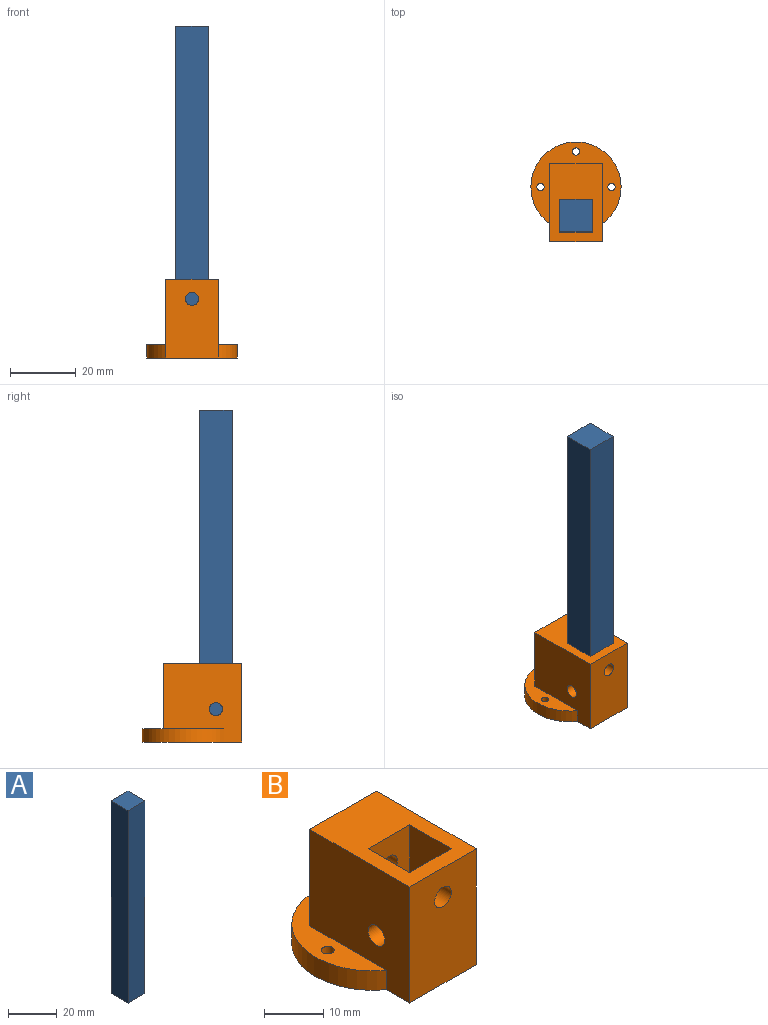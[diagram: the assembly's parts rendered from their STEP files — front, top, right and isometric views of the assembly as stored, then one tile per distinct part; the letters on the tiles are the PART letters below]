
ASSEMBLY  parts=2 mates=1
PART A: 6 faces, bbox 9.9x9.9x97.1 mm
  f0: plane 97.1x9.9mm, normal (1,0,0), area 961.3mm2, adj f1,f3,f4,f5
  f1: plane 97.1x9.9mm, normal (0,1,0), area 961.3mm2, adj f0,f2,f4,f5
  f2: plane 97.1x9.9mm, normal (-1,0,0), area 961.3mm2, adj f1,f3,f4,f5
  f3: plane 97.1x9.9mm, normal (0,-1,0), area 961.3mm2, adj f0,f2,f4,f5
  f4: plane 9.9x9.9mm, normal (0,0,1), area 98mm2, adj f0,f1,f2,f3
  f5: plane 9.9x9.9mm, normal (0,0,-1), area 98mm2, adj f0,f1,f2,f3
PART B: 25 faces, bbox 27.5x30.5x24 mm
  f0: cylinder r=1.11mm len=2.3mm, axis (0,0,-1), area 16mm2, adj f8,f24
  f1: plane 27.47x24.94mm, normal (0,0,1), area 261.6mm2, adj f3,f5,f6,f7,f10,f11,f22
  f2: plane 9.9x9.9mm, normal (0,0,1), area 85.4mm2, adj f13,f14,f15,f16,f23
  f3: cylinder r=13.74mm len=27.47mm, axis (0,0,-1), area 277.4mm2, adj f1,f8,f10,f11
  f4: cylinder r=5mm len=10mm, axis (0,0,-1), area 15.7mm2, adj f8,f9
  f5: cylinder r=1.11mm len=4mm, axis (0,0,-1), area 27.9mm2, adj f1,f8
  f6: cylinder r=1.11mm len=4mm, axis (0,0,-1), area 27.9mm2, adj f1,f8
  f7: cylinder r=1.11mm len=4mm, axis (0,0,-1), area 27.9mm2, adj f1,f8
  f8: plane 30.47x27.47mm, normal (0,0,-1), area 559.2mm2, adj f0,f3,f4,f5,f6,f7,f10,f11
  f9: plane 10x10mm, normal (0,0,-1), area 78.5mm2, adj f4
  f10: plane 24x23.9mm, normal (1,0,0), area 487.6mm2, adj f1,f3,f8,f12,f17,f19,f22
  f11: plane 24x23.9mm, normal (-1,0,0), area 487.6mm2, adj f1,f3,f8,f12,f17,f18,f22
  f12: plane 24x15.9mm, normal (0,-1,0), area 369mm2, adj f8,f10,f11,f17,f21
  f13: plane 20x9.9mm, normal (0,-1,0), area 185.4mm2, adj f2,f14,f16,f17,f20
  f14: plane 20x9.9mm, normal (-1,0,0), area 185.4mm2, adj f2,f13,f15,f17,f19
  f15: plane 20x9.9mm, normal (0,1,0), area 185.4mm2, adj f2,f14,f16,f17,f21
  f16: plane 20x9.9mm, normal (1,0,0), area 185.4mm2, adj f2,f13,f15,f17,f18
  f17: plane 23.9x15.9mm, normal (0,0,1), area 282mm2, adj f10,f11,f12,f13,f14,f15,f16,f22
  f18: cylinder r=2mm len=4mm, axis (1,0,0), area 37.7mm2, adj f11,f16
  f19: cylinder r=2mm len=4mm, axis (1,0,0), area 37.7mm2, adj f10,f14
  f20: cylinder r=2mm len=11mm, axis (0,1,0), area 138.2mm2, adj f13,f22
  f21: cylinder r=2mm len=4mm, axis (0,1,0), area 37.7mm2, adj f12,f15
  f22: plane 20x15.9mm, normal (0,1,0), area 305.4mm2, adj f1,f10,f11,f17,f20
  f23: cylinder r=2mm len=4mm, axis (0,0,1), area 21.4mm2, adj f2,f24
  f24: plane 4x4mm, normal (0,0,1), area 8.7mm2, adj f0,f23
PLACE A t=(-29.37,-11.48,8.22)mm
PLACE B t=(-29.37,-2.7,-42.33)mm
MATE fastened B.f2 <-> A.f5  axis (0,0,1) through (-29.37,-16.43,-40.33)mm
